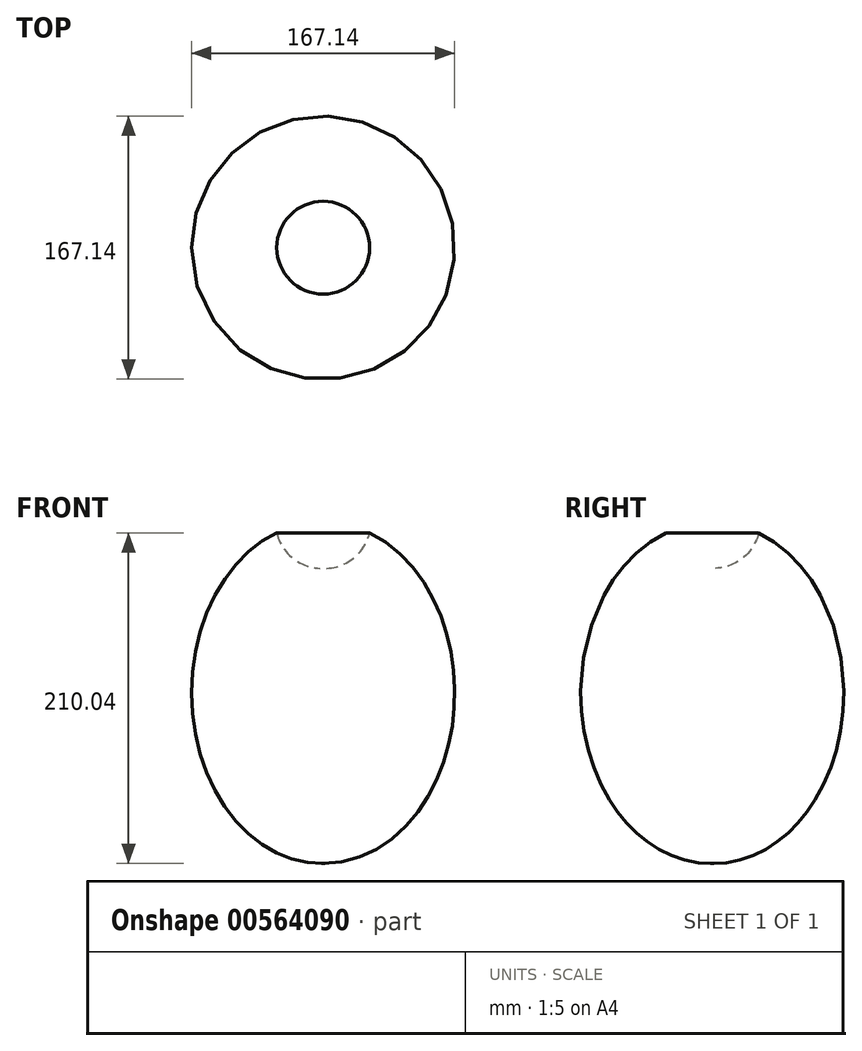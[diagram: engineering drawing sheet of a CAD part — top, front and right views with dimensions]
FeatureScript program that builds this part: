
annotation { "Feature Type Name" : "Feature", "Feature Type Description" : "" }
export const myFeature = defineFeature(function(context is Context, id is Id, definition is map)
    precondition{}
    {
        {
            var Q0;
            Q0=qCreatedBy(makeId("Front.planeOp"),FACE);
            var sketch = newSketch(context, id + "F0", { "sketchPlane" : qUnion([Q0])});
            skEllipticalArc(sketch, "E0", {});
            skArc(sketch, "E1", {"start": v(1, 189.51) * mm, "mid": v(-29.25, 160.28) * mm, "end": v(1, 131.05) * mm});
            skLineSegment(sketch, "E2", {"start": v(1, 189.51) * mm, "end": v(1, -56.4) * mm});
            const initialGuessF0  = {"E0": [0, 0.05194086581468606, 0, -1, 0.10834143310785264, 0.08258431527825096, 3.1295809653427717, 0.012011688247021295]};
            skSetInitialGuess(sketch, initialGuessF0);
            skSolve(sketch);
        }
        {
            var Q0;
            {var subQ0=sQuery(id+"F0.wireOp",EDGE,"E2");var subQ1=sQuery(id+"F0.wireOp",EDGE,"E0");var subQ2=makeQuery(id+"F0.imprint","INTERSECT",VERTEX,{"disambiguationData":[OD(1.0)],"derivedFrom":[subQ1,subQ0]});Q0=makeQuery(id+"F0.imprint","IMPRINT",FACE,{"disambiguationData":[TD([[makeQuery(id+"F0.imprint","IMPRINT",EDGE,{"disambiguationData":[TD([[subQ2,1.0]])],"derivedFrom":subQ1}),1.0]])]});}
            var Q1;
            Q1 = qSketchRegion(id + "F0", true);
            var Q2;
            {var subQ0=sQuery(id+"F0.wireOp",EDGE,"E2");var subQ1=sQuery(id+"F0.wireOp",EDGE,"E0");var subQ2=makeQuery(id+"F0.imprint","INTERSECT",VERTEX,{"disambiguationData":[OD(0.0)],"derivedFrom":[subQ1,subQ0]});Q2=makeQuery(id+"F0.imprint","IMPRINT",FACE,{"disambiguationData":[TD([[makeQuery(id+"F0.imprint","IMPRINT",EDGE,{"disambiguationData":[TD([[subQ2,-1.0]])],"derivedFrom":subQ1}),1.0]])]});}
            var Q3;
            {var subQ0=sQuery(id+"F0.wireOp",EDGE,"E2");var subQ1=sQuery(id+"F0.wireOp",EDGE,"E0");var subQ2=makeQuery(id+"F0.imprint","INTERSECT",VERTEX,{"disambiguationData":[OD(0.0)],"derivedFrom":[subQ1,subQ0]});Q3=makeQuery(id+"F0.imprint","IMPRINT",FACE,{"disambiguationData":[TD([[makeQuery(id+"F0.imprint","IMPRINT",EDGE,{"disambiguationData":[TD([[subQ2,-1.0]])],"derivedFrom":subQ1}),-1.0]])]});}
            var Q4;
            Q4=sQuery(id+"F0.wireOp",EDGE,"E2");
            revolve(context, id + "F1", {"entities" : qUnion([Q0, Q1, Q2, Q3]), "axis" : qUnion([Q4]), "revolveType" : RevolveType.FULL});
        }
    });
